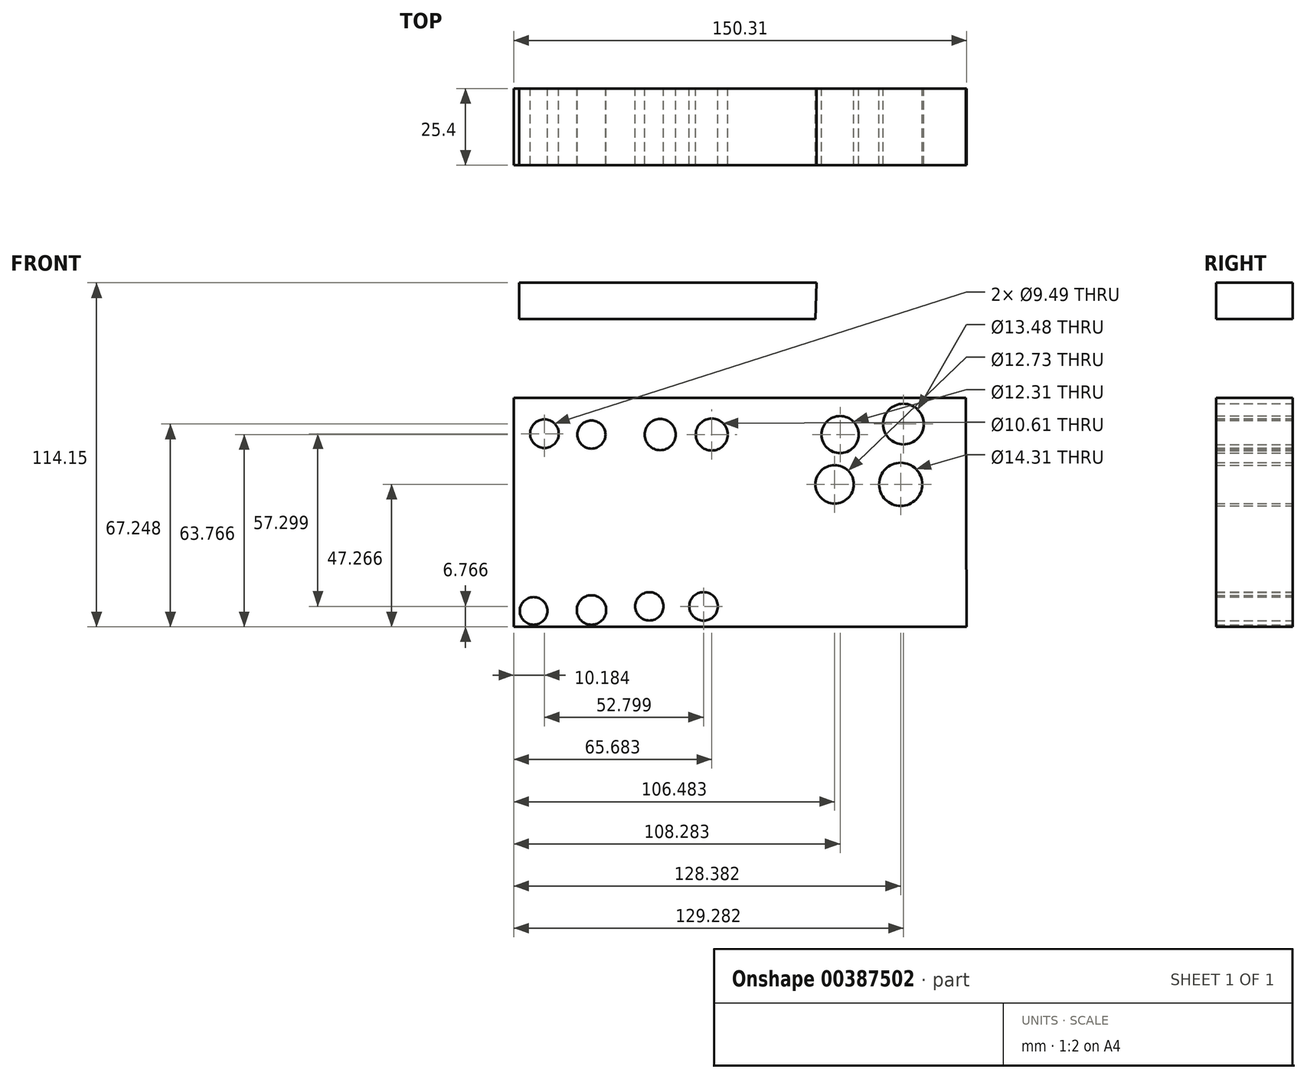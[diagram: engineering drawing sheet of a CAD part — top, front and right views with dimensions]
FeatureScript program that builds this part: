
annotation { "Feature Type Name" : "Feature", "Feature Type Description" : "" }
export const myFeature = defineFeature(function(context is Context, id is Id, definition is map)
    precondition{}
    {
        {
            var Q0;
            Q0=qCreatedBy(makeId("Front.planeOp"),FACE);
            var sketch = newSketch(context, id + "F0", { "sketchPlane" : qUnion([Q0])});
            skLineSegment(sketch, "E0", {"start": v(-77.24, 38.15) * mm, "end": v(-77.24, 26.16) * mm});
            skLineSegment(sketch, "E1", {"start": v(-77.24, 38.15) * mm, "end": v(21.46, 38.15) * mm});
            skLineSegment(sketch, "E2", {"start": v(-77.24, 26.16) * mm, "end": v(21.07, 26.16) * mm});
            skLineSegment(sketch, "E3", {"start": v(21.46, 38.15) * mm, "end": v(21.07, 26.16) * mm});
            skLineSegment(sketch, "E4", {"start": v(-79, 0) * mm, "end": v(71.02, 0) * mm});
            skLineSegment(sketch, "E5", {"start": v(-79, 0) * mm, "end": v(-79, -76) * mm});
            skLineSegment(sketch, "E6", {"start": v(-79, -76) * mm, "end": v(71.32, -76) * mm});
            skLineSegment(sketch, "E7", {"start": v(71.02, 0) * mm, "end": v(71.32, -76) * mm});
            skCircle(sketch, "E8", {"center": v(-68.8, -11.93) * mm, "radius": 4.74 * mm});
            skCircle(sketch, "E9", {"center": v(-53.2, -12.23) * mm, "radius": 4.67 * mm});
            skCircle(sketch, "E10", {"center": v(-72.4, -70.73) * mm, "radius": 4.58 * mm});
            skCircle(sketch, "E11", {"center": v(-53.2, -70.43) * mm, "radius": 4.88 * mm});
            skCircle(sketch, "E12", {"center": v(-30.4, -12.23) * mm, "radius": 5.16 * mm});
            skCircle(sketch, "E13", {"center": v(-13.3, -12.23) * mm, "radius": 5.3 * mm});
            skCircle(sketch, "E14", {"center": v(-34, -69.23) * mm, "radius": 4.7 * mm});
            skCircle(sketch, "E15", {"center": v(-16, -69.23) * mm, "radius": 4.74 * mm});
            skCircle(sketch, "E16", {"center": v(29.3, -12.23) * mm, "radius": 6.16 * mm});
            skCircle(sketch, "E17", {"center": v(27.5, -28.73) * mm, "radius": 6.36 * mm});
            skCircle(sketch, "E18", {"center": v(50.3, -8.75) * mm, "radius": 6.74 * mm});
            skPoint(sketch, "E19.center.orphan", {"position": v(49.4, -12.23) * mm});
            skCircle(sketch, "E20", {"center": v(49.4, -28.73) * mm, "radius": 7.16 * mm});
            skSolve(sketch);
        }
        {
            var Q0;
            Q0 = qSketchRegion(id + "F0", true);
            extrude(context, id + "F1", {"entities" : qUnion([Q0]), "depth" : 25.4 * mm});
        }
    });
